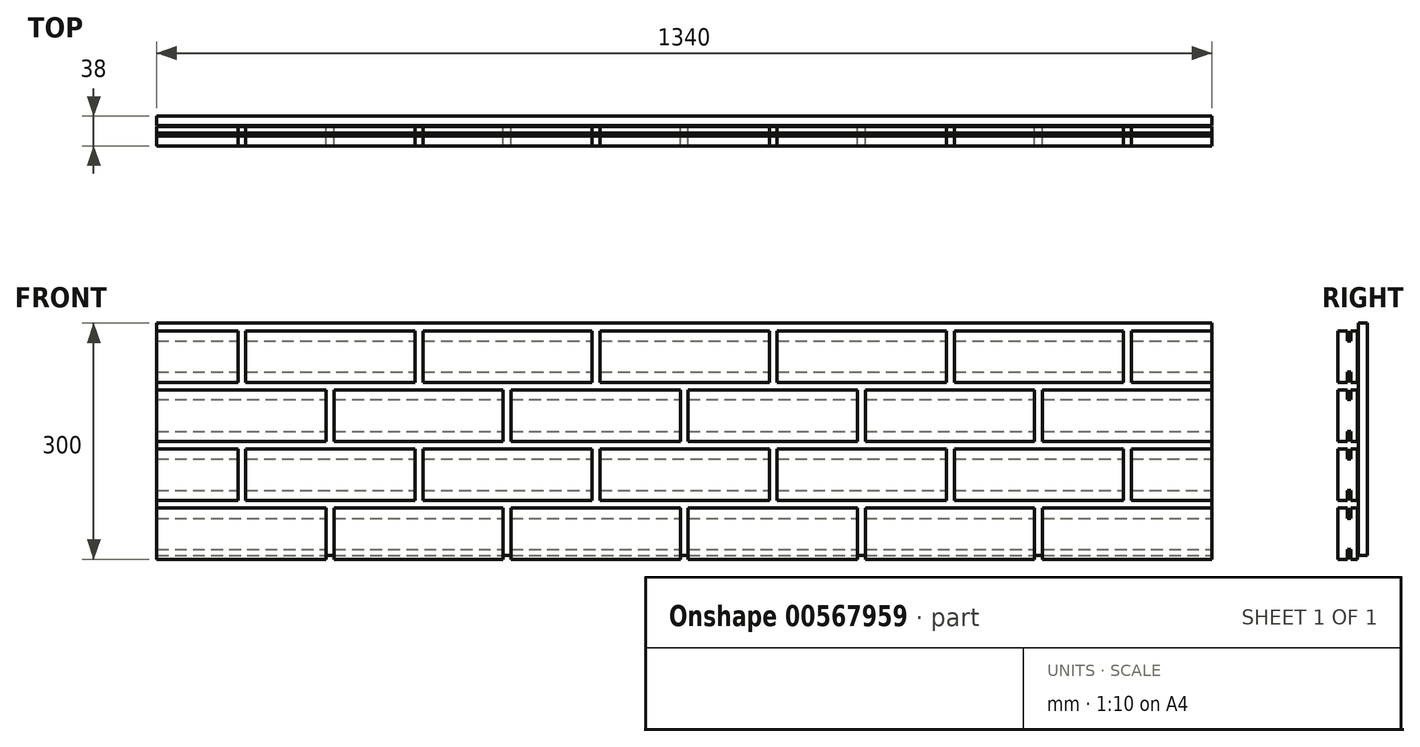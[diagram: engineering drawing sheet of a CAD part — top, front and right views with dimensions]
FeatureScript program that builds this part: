
annotation { "Feature Type Name" : "Feature", "Feature Type Description" : "" }
export const myFeature = defineFeature(function(context is Context, id is Id, definition is map)
    precondition{}
    {
        {
            var Q0;
            Q0=qCreatedBy(makeId("Front.planeOp"),FACE);
            var sketch = newSketch(context, id + "F0", { "sketchPlane" : qUnion([Q0])});
            skLineSegment(sketch, "E0", {"start": v(-1965.67, 0) * mm, "end": v(-1750.67, 0) * mm});
            skLineSegment(sketch, "E1", {"start": v(-1750.67, 0) * mm, "end": v(-1750.67, 65) * mm});
            skLineSegment(sketch, "E2", {"start": v(-1750.67, 65) * mm, "end": v(-1965.67, 65) * mm});
            skLineSegment(sketch, "E3", {"start": v(-1965.67, 65) * mm, "end": v(-1965.67, 0) * mm});
            skLineSegment(sketch, "E4", {"start": v(-1975.67, 0) * mm, "end": v(-2190.67, 0) * mm});
            skLineSegment(sketch, "E5", {"start": v(-2190.67, 0) * mm, "end": v(-2190.67, 65) * mm});
            skLineSegment(sketch, "E6", {"start": v(-2190.67, 65) * mm, "end": v(-1975.67, 65) * mm});
            skLineSegment(sketch, "E7", {"start": v(-1975.67, 65) * mm, "end": v(-1975.67, 0) * mm});
            skLineSegment(sketch, "E8", {"start": v(-2200.67, 0) * mm, "end": v(-2415.67, 0) * mm});
            skLineSegment(sketch, "E9", {"start": v(-2415.67, 0) * mm, "end": v(-2415.67, 65) * mm});
            skLineSegment(sketch, "E10", {"start": v(-2415.67, 65) * mm, "end": v(-2200.67, 65) * mm});
            skLineSegment(sketch, "E11", {"start": v(-2200.67, 65) * mm, "end": v(-2200.67, 0) * mm});
            skLineSegment(sketch, "E12", {"start": v(-2087.7, 139.95) * mm, "end": v(-2302.7, 139.95) * mm});
            skLineSegment(sketch, "E13", {"start": v(-2302.7, 139.95) * mm, "end": v(-2302.7, 74.95) * mm});
            skLineSegment(sketch, "E14", {"start": v(-2302.7, 74.95) * mm, "end": v(-2087.7, 74.95) * mm});
            skLineSegment(sketch, "E15", {"start": v(-2087.7, 74.95) * mm, "end": v(-2087.7, 139.95) * mm});
            skLineSegment(sketch, "E16", {"start": v(-2077.7, 139.95) * mm, "end": v(-1862.7, 139.95) * mm});
            skLineSegment(sketch, "E17", {"start": v(-1862.7, 139.95) * mm, "end": v(-1862.7, 74.95) * mm});
            skLineSegment(sketch, "E18", {"start": v(-1862.7, 74.95) * mm, "end": v(-2077.7, 74.95) * mm});
            skLineSegment(sketch, "E19", {"start": v(-2077.7, 74.95) * mm, "end": v(-2077.7, 139.95) * mm});
            skLineSegment(sketch, "E20", {"start": v(-1852.7, 139.95) * mm, "end": v(-1637.7, 139.95) * mm});
            skLineSegment(sketch, "E21", {"start": v(-1637.7, 139.95) * mm, "end": v(-1637.7, 74.95) * mm});
            skLineSegment(sketch, "E22", {"start": v(-1637.7, 74.95) * mm, "end": v(-1852.7, 74.95) * mm});
            skLineSegment(sketch, "E23", {"start": v(-1852.7, 74.95) * mm, "end": v(-1852.7, 139.95) * mm});
            skLineSegment(sketch, "E24", {"start": v(-2415.7, 139.95) * mm, "end": v(-2312.7, 139.95) * mm});
            skLineSegment(sketch, "E25", {"start": v(-2312.7, 139.95) * mm, "end": v(-2312.7, 74.95) * mm});
            skLineSegment(sketch, "E26", {"start": v(-2312.7, 74.95) * mm, "end": v(-2415.7, 74.95) * mm});
            skLineSegment(sketch, "E27", {"start": v(-2415.7, 74.95) * mm, "end": v(-2415.7, 139.95) * mm});
            skLineSegment(sketch, "E28", {"start": v(-1965.67, 215) * mm, "end": v(-1750.67, 215) * mm});
            skLineSegment(sketch, "E29", {"start": v(-1750.67, 215) * mm, "end": v(-1750.67, 150) * mm});
            skLineSegment(sketch, "E30", {"start": v(-1750.67, 150) * mm, "end": v(-1965.67, 150) * mm});
            skLineSegment(sketch, "E31", {"start": v(-1965.67, 150) * mm, "end": v(-1965.67, 215) * mm});
            skLineSegment(sketch, "E32", {"start": v(-1975.67, 215) * mm, "end": v(-2190.67, 215) * mm});
            skLineSegment(sketch, "E33", {"start": v(-2190.67, 215) * mm, "end": v(-2190.67, 150) * mm});
            skLineSegment(sketch, "E34", {"start": v(-2190.67, 150) * mm, "end": v(-1975.67, 150) * mm});
            skLineSegment(sketch, "E35", {"start": v(-1975.67, 150) * mm, "end": v(-1975.67, 215) * mm});
            skLineSegment(sketch, "E36", {"start": v(-2200.67, 215) * mm, "end": v(-2415.67, 215) * mm});
            skLineSegment(sketch, "E37", {"start": v(-2415.67, 215) * mm, "end": v(-2415.67, 150) * mm});
            skLineSegment(sketch, "E38", {"start": v(-2415.67, 150) * mm, "end": v(-2200.67, 150) * mm});
            skLineSegment(sketch, "E39", {"start": v(-2200.67, 150) * mm, "end": v(-2200.67, 215) * mm});
            skLineSegment(sketch, "E40", {"start": v(-2087.7, 224.95) * mm, "end": v(-2302.7, 224.95) * mm});
            skLineSegment(sketch, "E41", {"start": v(-2302.7, 224.95) * mm, "end": v(-2302.7, 289.95) * mm});
            skLineSegment(sketch, "E42", {"start": v(-2302.7, 289.95) * mm, "end": v(-2087.7, 289.95) * mm});
            skLineSegment(sketch, "E43", {"start": v(-2087.7, 289.95) * mm, "end": v(-2087.7, 224.95) * mm});
            skLineSegment(sketch, "E44", {"start": v(-2077.7, 224.95) * mm, "end": v(-1862.7, 224.95) * mm});
            skLineSegment(sketch, "E45", {"start": v(-1862.7, 224.95) * mm, "end": v(-1862.7, 289.95) * mm});
            skLineSegment(sketch, "E46", {"start": v(-1862.7, 289.95) * mm, "end": v(-2077.7, 289.95) * mm});
            skLineSegment(sketch, "E47", {"start": v(-2077.7, 289.95) * mm, "end": v(-2077.7, 224.95) * mm});
            skLineSegment(sketch, "E48", {"start": v(-1852.7, 224.95) * mm, "end": v(-1637.7, 224.95) * mm});
            skLineSegment(sketch, "E49", {"start": v(-1637.7, 224.95) * mm, "end": v(-1637.7, 289.95) * mm});
            skLineSegment(sketch, "E50", {"start": v(-1637.7, 289.95) * mm, "end": v(-1852.7, 289.95) * mm});
            skLineSegment(sketch, "E51", {"start": v(-1852.7, 289.95) * mm, "end": v(-1852.7, 224.95) * mm});
            skLineSegment(sketch, "E52", {"start": v(-2415.7, 224.95) * mm, "end": v(-2312.7, 224.95) * mm});
            skLineSegment(sketch, "E53", {"start": v(-2312.7, 224.95) * mm, "end": v(-2312.7, 289.95) * mm});
            skLineSegment(sketch, "E54", {"start": v(-2312.7, 289.95) * mm, "end": v(-2415.7, 289.95) * mm});
            skLineSegment(sketch, "E55", {"start": v(-2415.7, 289.95) * mm, "end": v(-2415.7, 224.95) * mm});
            skLineSegment(sketch, "E56", {"start": v(-1515.67, 0) * mm, "end": v(-1300.67, 0) * mm});
            skLineSegment(sketch, "E57", {"start": v(-1300.67, 0) * mm, "end": v(-1300.67, 65) * mm});
            skLineSegment(sketch, "E58", {"start": v(-1300.67, 65) * mm, "end": v(-1515.67, 65) * mm});
            skLineSegment(sketch, "E59", {"start": v(-1515.67, 65) * mm, "end": v(-1515.67, 0) * mm});
            skLineSegment(sketch, "E60", {"start": v(-1525.67, 0) * mm, "end": v(-1740.67, 0) * mm});
            skLineSegment(sketch, "E61", {"start": v(-1740.67, 0) * mm, "end": v(-1740.67, 65) * mm});
            skLineSegment(sketch, "E62", {"start": v(-1740.67, 65) * mm, "end": v(-1525.67, 65) * mm});
            skLineSegment(sketch, "E63", {"start": v(-1525.67, 65) * mm, "end": v(-1525.67, 0) * mm});
            skLineSegment(sketch, "E64", {"start": v(-1515.67, 215) * mm, "end": v(-1300.67, 215) * mm});
            skLineSegment(sketch, "E65", {"start": v(-1300.67, 215) * mm, "end": v(-1300.67, 150) * mm});
            skLineSegment(sketch, "E66", {"start": v(-1300.67, 150) * mm, "end": v(-1515.67, 150) * mm});
            skLineSegment(sketch, "E67", {"start": v(-1515.67, 150) * mm, "end": v(-1515.67, 215) * mm});
            skLineSegment(sketch, "E68", {"start": v(-1525.67, 215) * mm, "end": v(-1740.67, 215) * mm});
            skLineSegment(sketch, "E69", {"start": v(-1740.67, 215) * mm, "end": v(-1740.67, 150) * mm});
            skLineSegment(sketch, "E70", {"start": v(-1740.67, 150) * mm, "end": v(-1525.67, 150) * mm});
            skLineSegment(sketch, "E71", {"start": v(-1525.67, 150) * mm, "end": v(-1525.67, 215) * mm});
            skLineSegment(sketch, "E72", {"start": v(-1290.67, 0) * mm, "end": v(-1075.67, 0) * mm});
            skLineSegment(sketch, "E73", {"start": v(-1075.67, 0) * mm, "end": v(-1075.67, 65) * mm});
            skLineSegment(sketch, "E74", {"start": v(-1075.67, 65) * mm, "end": v(-1290.67, 65) * mm});
            skLineSegment(sketch, "E75", {"start": v(-1290.67, 65) * mm, "end": v(-1290.67, 0) * mm});
            skLineSegment(sketch, "E76", {"start": v(-1290.67, 150) * mm, "end": v(-1075.67, 150) * mm});
            skLineSegment(sketch, "E77", {"start": v(-1075.67, 150) * mm, "end": v(-1075.67, 215) * mm});
            skLineSegment(sketch, "E78", {"start": v(-1075.67, 215) * mm, "end": v(-1290.67, 215) * mm});
            skLineSegment(sketch, "E79", {"start": v(-1290.67, 215) * mm, "end": v(-1290.67, 150) * mm});
            skLineSegment(sketch, "E80", {"start": v(-1627.7, 139.95) * mm, "end": v(-1412.7, 139.95) * mm});
            skLineSegment(sketch, "E81", {"start": v(-1412.7, 139.95) * mm, "end": v(-1412.7, 74.95) * mm});
            skLineSegment(sketch, "E82", {"start": v(-1412.7, 74.95) * mm, "end": v(-1627.7, 74.95) * mm});
            skLineSegment(sketch, "E83", {"start": v(-1627.7, 74.95) * mm, "end": v(-1627.7, 139.95) * mm});
            skLineSegment(sketch, "E84", {"start": v(-1627.7, 224.95) * mm, "end": v(-1412.7, 224.95) * mm});
            skLineSegment(sketch, "E85", {"start": v(-1412.7, 224.95) * mm, "end": v(-1412.7, 289.95) * mm});
            skLineSegment(sketch, "E86", {"start": v(-1412.7, 289.95) * mm, "end": v(-1627.7, 289.95) * mm});
            skLineSegment(sketch, "E87", {"start": v(-1627.7, 289.95) * mm, "end": v(-1627.7, 224.95) * mm});
            skLineSegment(sketch, "E88", {"start": v(-1402.7, 139.95) * mm, "end": v(-1187.7, 139.95) * mm});
            skLineSegment(sketch, "E89", {"start": v(-1187.7, 139.95) * mm, "end": v(-1187.7, 74.95) * mm});
            skLineSegment(sketch, "E90", {"start": v(-1187.7, 74.95) * mm, "end": v(-1402.7, 74.95) * mm});
            skLineSegment(sketch, "E91", {"start": v(-1402.7, 74.95) * mm, "end": v(-1402.7, 139.95) * mm});
            skLineSegment(sketch, "E92", {"start": v(-1402.7, 224.95) * mm, "end": v(-1187.7, 224.95) * mm});
            skLineSegment(sketch, "E93", {"start": v(-1187.7, 224.95) * mm, "end": v(-1187.7, 289.95) * mm});
            skLineSegment(sketch, "E94", {"start": v(-1187.7, 289.95) * mm, "end": v(-1402.7, 289.95) * mm});
            skLineSegment(sketch, "E95", {"start": v(-1402.7, 289.95) * mm, "end": v(-1402.7, 224.95) * mm});
            skLineSegment(sketch, "E96", {"start": v(-1177.7, 139.95) * mm, "end": v(-1075.67, 139.95) * mm});
            skLineSegment(sketch, "E97", {"start": v(-1075.67, 139.95) * mm, "end": v(-1075.67, 74.95) * mm});
            skLineSegment(sketch, "E98", {"start": v(-1075.67, 74.95) * mm, "end": v(-1177.7, 74.95) * mm});
            skLineSegment(sketch, "E99", {"start": v(-1177.7, 74.95) * mm, "end": v(-1177.7, 139.95) * mm});
            skLineSegment(sketch, "E100", {"start": v(-1177.7, 224.95) * mm, "end": v(-1075.67, 224.95) * mm});
            skLineSegment(sketch, "E101", {"start": v(-1075.67, 224.95) * mm, "end": v(-1075.67, 289.95) * mm});
            skLineSegment(sketch, "E102", {"start": v(-1075.67, 289.95) * mm, "end": v(-1177.7, 289.95) * mm});
            skLineSegment(sketch, "E103", {"start": v(-1177.7, 289.95) * mm, "end": v(-1177.7, 224.95) * mm});
            skLineSegment(sketch, "E104", {"start": v(-2415.67, 5) * mm, "end": v(-1075.67, 5) * mm});
            skLineSegment(sketch, "E105", {"start": v(-1075.67, 5) * mm, "end": v(-1075.67, 300) * mm});
            skLineSegment(sketch, "E106", {"start": v(-1075.67, 300) * mm, "end": v(-2415.67, 300) * mm});
            skLineSegment(sketch, "E107", {"start": v(-2415.67, 300) * mm, "end": v(-2415.67, 5) * mm});
            skSolve(sketch);
        }
        {
            var Q0;
            {var subQ0=sQuery(id+"F0.wireOp",EDGE,"E8");Q0=makeQuery(id+"F0.imprint","IMPRINT",FACE,{"disambiguationData":[TD([[makeQuery(id+"F0.imprint","IMPRINT",EDGE,{"derivedFrom":subQ0}),-1.0]])]});}
            var Q1;
            {var subQ0=sQuery(id+"F0.wireOp",EDGE,"E4");Q1=makeQuery(id+"F0.imprint","IMPRINT",FACE,{"disambiguationData":[TD([[makeQuery(id+"F0.imprint","IMPRINT",EDGE,{"derivedFrom":subQ0}),-1.0]])]});}
            var Q2;
            {var subQ0=sQuery(id+"F0.wireOp",EDGE,"E0");Q2=makeQuery(id+"F0.imprint","IMPRINT",FACE,{"disambiguationData":[TD([[makeQuery(id+"F0.imprint","IMPRINT",EDGE,{"derivedFrom":subQ0}),1.0]])]});}
            var Q3;
            {var subQ0=sQuery(id+"F0.wireOp",EDGE,"E60");Q3=makeQuery(id+"F0.imprint","IMPRINT",FACE,{"disambiguationData":[TD([[makeQuery(id+"F0.imprint","IMPRINT",EDGE,{"derivedFrom":subQ0}),-1.0]])]});}
            var Q4;
            {var subQ0=sQuery(id+"F0.wireOp",EDGE,"E56");Q4=makeQuery(id+"F0.imprint","IMPRINT",FACE,{"disambiguationData":[TD([[makeQuery(id+"F0.imprint","IMPRINT",EDGE,{"derivedFrom":subQ0}),1.0]])]});}
            var Q5;
            {var subQ0=sQuery(id+"F0.wireOp",EDGE,"E72");Q5=makeQuery(id+"F0.imprint","IMPRINT",FACE,{"disambiguationData":[TD([[makeQuery(id+"F0.imprint","IMPRINT",EDGE,{"derivedFrom":subQ0}),1.0]])]});}
            var Q6;
            {var subQ0=sQuery(id+"F0.wireOp",EDGE,"E74");Q6=makeQuery(id+"F0.imprint","IMPRINT",FACE,{"disambiguationData":[TD([[makeQuery(id+"F0.imprint","IMPRINT",EDGE,{"derivedFrom":subQ0}),1.0]])]});}
            var Q7;
            {var subQ0=sQuery(id+"F0.wireOp",EDGE,"E58");Q7=makeQuery(id+"F0.imprint","IMPRINT",FACE,{"disambiguationData":[TD([[makeQuery(id+"F0.imprint","IMPRINT",EDGE,{"derivedFrom":subQ0}),1.0]])]});}
            var Q8;
            {var subQ0=sQuery(id+"F0.wireOp",EDGE,"E62");Q8=makeQuery(id+"F0.imprint","IMPRINT",FACE,{"disambiguationData":[TD([[makeQuery(id+"F0.imprint","IMPRINT",EDGE,{"derivedFrom":subQ0}),-1.0]])]});}
            var Q9;
            {var subQ0=sQuery(id+"F0.wireOp",EDGE,"E2");Q9=makeQuery(id+"F0.imprint","IMPRINT",FACE,{"disambiguationData":[TD([[makeQuery(id+"F0.imprint","IMPRINT",EDGE,{"derivedFrom":subQ0}),1.0]])]});}
            var Q10;
            {var subQ0=sQuery(id+"F0.wireOp",EDGE,"E6");Q10=makeQuery(id+"F0.imprint","IMPRINT",FACE,{"disambiguationData":[TD([[makeQuery(id+"F0.imprint","IMPRINT",EDGE,{"derivedFrom":subQ0}),-1.0]])]});}
            var Q11;
            {var subQ0=sQuery(id+"F0.wireOp",EDGE,"E10");Q11=makeQuery(id+"F0.imprint","IMPRINT",FACE,{"disambiguationData":[TD([[makeQuery(id+"F0.imprint","IMPRINT",EDGE,{"derivedFrom":subQ0}),-1.0]])]});}
            var Q12;
            {var subQ0=sQuery(id+"F0.wireOp",EDGE,"E25");Q12=makeQuery(id+"F0.imprint","IMPRINT",FACE,{"disambiguationData":[TD([[makeQuery(id+"F0.imprint","IMPRINT",EDGE,{"derivedFrom":subQ0}),-1.0]])]});}
            var Q13;
            Q13=makeQuery(id+"F0.imprint","IMPRINT",FACE,{"disambiguationData":[TD([[makeQuery(id+"F0.imprint","IMPRINT",EDGE,{"derivedFrom":sQuery(id+"F0.wireOp",EDGE,"E12")}),1.0]])]});
            var Q14;
            Q14=makeQuery(id+"F0.imprint","IMPRINT",FACE,{"disambiguationData":[TD([[makeQuery(id+"F0.imprint","IMPRINT",EDGE,{"derivedFrom":sQuery(id+"F0.wireOp",EDGE,"E16")}),-1.0]])]});
            var Q15;
            Q15=makeQuery(id+"F0.imprint","IMPRINT",FACE,{"disambiguationData":[TD([[makeQuery(id+"F0.imprint","IMPRINT",EDGE,{"derivedFrom":sQuery(id+"F0.wireOp",EDGE,"E20")}),-1.0]])]});
            var Q16;
            Q16=makeQuery(id+"F0.imprint","IMPRINT",FACE,{"disambiguationData":[TD([[makeQuery(id+"F0.imprint","IMPRINT",EDGE,{"derivedFrom":sQuery(id+"F0.wireOp",EDGE,"E80")}),-1.0]])]});
            var Q17;
            Q17=makeQuery(id+"F0.imprint","IMPRINT",FACE,{"disambiguationData":[TD([[makeQuery(id+"F0.imprint","IMPRINT",EDGE,{"derivedFrom":sQuery(id+"F0.wireOp",EDGE,"E88")}),-1.0]])]});
            var Q18;
            {var subQ0=sQuery(id+"F0.wireOp",EDGE,"E96");Q18=makeQuery(id+"F0.imprint","IMPRINT",FACE,{"disambiguationData":[TD([[makeQuery(id+"F0.imprint","IMPRINT",EDGE,{"derivedFrom":subQ0}),-1.0]])]});}
            var Q19;
            {var subQ0=sQuery(id+"F0.wireOp",EDGE,"E76");Q19=makeQuery(id+"F0.imprint","IMPRINT",FACE,{"disambiguationData":[TD([[makeQuery(id+"F0.imprint","IMPRINT",EDGE,{"derivedFrom":subQ0}),1.0]])]});}
            var Q20;
            Q20=makeQuery(id+"F0.imprint","IMPRINT",FACE,{"disambiguationData":[TD([[makeQuery(id+"F0.imprint","IMPRINT",EDGE,{"derivedFrom":sQuery(id+"F0.wireOp",EDGE,"E64")}),-1.0]])]});
            var Q21;
            Q21=makeQuery(id+"F0.imprint","IMPRINT",FACE,{"disambiguationData":[TD([[makeQuery(id+"F0.imprint","IMPRINT",EDGE,{"derivedFrom":sQuery(id+"F0.wireOp",EDGE,"E68")}),1.0]])]});
            var Q22;
            Q22=makeQuery(id+"F0.imprint","IMPRINT",FACE,{"disambiguationData":[TD([[makeQuery(id+"F0.imprint","IMPRINT",EDGE,{"derivedFrom":sQuery(id+"F0.wireOp",EDGE,"E28")}),-1.0]])]});
            var Q23;
            {var subQ0=sQuery(id+"F0.wireOp",EDGE,"E36");Q23=makeQuery(id+"F0.imprint","IMPRINT",FACE,{"disambiguationData":[TD([[makeQuery(id+"F0.imprint","IMPRINT",EDGE,{"derivedFrom":subQ0}),1.0]])]});}
            var Q24;
            Q24=makeQuery(id+"F0.imprint","IMPRINT",FACE,{"disambiguationData":[TD([[makeQuery(id+"F0.imprint","IMPRINT",EDGE,{"derivedFrom":sQuery(id+"F0.wireOp",EDGE,"E32")}),1.0]])]});
            var Q25;
            {var subQ0=sQuery(id+"F0.wireOp",EDGE,"E53");Q25=makeQuery(id+"F0.imprint","IMPRINT",FACE,{"disambiguationData":[TD([[makeQuery(id+"F0.imprint","IMPRINT",EDGE,{"derivedFrom":subQ0}),1.0]])]});}
            var Q26;
            Q26=makeQuery(id+"F0.imprint","IMPRINT",FACE,{"disambiguationData":[TD([[makeQuery(id+"F0.imprint","IMPRINT",EDGE,{"derivedFrom":sQuery(id+"F0.wireOp",EDGE,"E40")}),-1.0]])]});
            var Q27;
            Q27=makeQuery(id+"F0.imprint","IMPRINT",FACE,{"disambiguationData":[TD([[makeQuery(id+"F0.imprint","IMPRINT",EDGE,{"derivedFrom":sQuery(id+"F0.wireOp",EDGE,"E44")}),1.0]])]});
            var Q28;
            Q28=makeQuery(id+"F0.imprint","IMPRINT",FACE,{"disambiguationData":[TD([[makeQuery(id+"F0.imprint","IMPRINT",EDGE,{"derivedFrom":sQuery(id+"F0.wireOp",EDGE,"E48")}),1.0]])]});
            var Q29;
            Q29=makeQuery(id+"F0.imprint","IMPRINT",FACE,{"disambiguationData":[TD([[makeQuery(id+"F0.imprint","IMPRINT",EDGE,{"derivedFrom":sQuery(id+"F0.wireOp",EDGE,"E84")}),1.0]])]});
            var Q30;
            Q30=makeQuery(id+"F0.imprint","IMPRINT",FACE,{"disambiguationData":[TD([[makeQuery(id+"F0.imprint","IMPRINT",EDGE,{"derivedFrom":sQuery(id+"F0.wireOp",EDGE,"E92")}),1.0]])]});
            var Q31;
            {var subQ0=sQuery(id+"F0.wireOp",EDGE,"E100");Q31=makeQuery(id+"F0.imprint","IMPRINT",FACE,{"disambiguationData":[TD([[makeQuery(id+"F0.imprint","IMPRINT",EDGE,{"derivedFrom":subQ0}),1.0]])]});}
            extrude(context, id + "F1", {"entities" : qUnion([Q0, Q1, Q2, Q3, Q4, Q5, Q6, Q7, Q8, Q9, Q10, Q11, Q12, Q13, Q14, Q15, Q16, Q17, Q18, Q19, Q20, Q21, Q22, Q23, Q24, Q25, Q26, Q27, Q28, Q29, Q30, Q31]), "depth" : 25 * mm, "offsetDistance" : 25 * mm});
        }
        {
            var Q0;
            Q0=makeQuery(id+"F1.opExtrude","SWEPT_FACE",FACE,{"disambiguationData":[OSD([sQuery(id+"F0.wireOp",EDGE,"E73"),sQuery(id+"F0.wireOp",EDGE,"E105")])]});
            cPlane(context, id + "F2", {"entities" : qUnion([Q0]), "cplaneType" : CPlaneType.OFFSET, "offset" : 0 * mm, "width" : 150 * mm, "height" : 150 * mm});
        }
        {
            var Q0;
            Q0=qCreatedBy(id+"F2.planeOp",FACE);
            var sketch = newSketch(context, id + "F3", { "sketchPlane" : qUnion([Q0])});
            skLineSegment(sketch, "E108.bottom", {"start": v(-12.5, 52.26) * mm, "end": v(-8.5, 52.26) * mm});
            skLineSegment(sketch, "E108.top", {"start": v(-12.5, 87.26) * mm, "end": v(-8.5, 87.26) * mm});
            skLineSegment(sketch, "E108.left", {"start": v(-12.5, 52.26) * mm, "end": v(-12.5, 87.26) * mm});
            skLineSegment(sketch, "E108.right", {"start": v(-8.5, 52.26) * mm, "end": v(-8.5, 87.26) * mm});
            skLineSegment(sketch, "E109.bottom", {"start": v(-12.5, 127.29) * mm, "end": v(-8.5, 127.29) * mm});
            skLineSegment(sketch, "E109.top", {"start": v(-12.5, 162.29) * mm, "end": v(-8.5, 162.29) * mm});
            skLineSegment(sketch, "E109.left", {"start": v(-12.5, 127.29) * mm, "end": v(-12.5, 162.29) * mm});
            skLineSegment(sketch, "E109.right", {"start": v(-8.5, 127.29) * mm, "end": v(-8.5, 162.29) * mm});
            skLineSegment(sketch, "E110.bottom", {"start": v(-12.5, 202.92) * mm, "end": v(-8.5, 202.92) * mm});
            skLineSegment(sketch, "E110.top", {"start": v(-12.5, 237.92) * mm, "end": v(-8.5, 237.92) * mm});
            skLineSegment(sketch, "E110.left", {"start": v(-12.5, 202.92) * mm, "end": v(-12.5, 237.92) * mm});
            skLineSegment(sketch, "E110.right", {"start": v(-8.5, 202.92) * mm, "end": v(-8.5, 237.92) * mm});
            skLineSegment(sketch, "E111.bottom", {"start": v(-12.5, 0) * mm, "end": v(-8.5, 0) * mm});
            skLineSegment(sketch, "E111.top", {"start": v(-12.5, 12.75) * mm, "end": v(-8.5, 12.75) * mm});
            skLineSegment(sketch, "E111.left", {"start": v(-12.5, 0) * mm, "end": v(-12.5, 12.75) * mm});
            skLineSegment(sketch, "E111.right", {"start": v(-8.5, 0) * mm, "end": v(-8.5, 12.75) * mm});
            skLineSegment(sketch, "E112.bottom", {"start": v(-12.5, 277.2) * mm, "end": v(-8.5, 277.2) * mm});
            skLineSegment(sketch, "E112.top", {"start": v(-12.5, 289.95) * mm, "end": v(-8.5, 289.95) * mm});
            skLineSegment(sketch, "E112.left", {"start": v(-12.5, 277.2) * mm, "end": v(-12.5, 289.95) * mm});
            skLineSegment(sketch, "E112.right", {"start": v(-8.5, 277.2) * mm, "end": v(-8.5, 289.95) * mm});
            skSolve(sketch);
        }
        {
            var Q0;
            Q0 = qSketchRegion(id + "F3", true);
            extrude(context, id + "F4", {"entities" : qUnion([Q0]), "operationType" : NewBodyOperationType.REMOVE, "endBound" : BoundingType.THROUGH_ALL, "oppositeDirection" : true, "depth" : 25 * mm, "offsetDistance" : 25 * mm});
        }
        {
            var Q0;
            Q0=qCreatedBy(id+"F2.planeOp",FACE);
            var sketch = newSketch(context, id + "F5", { "sketchPlane" : qUnion([Q0])});
            skLineSegment(sketch, "E113.bottom", {"start": v(1, 5) * mm, "end": v(13, 5) * mm});
            skLineSegment(sketch, "E113.top", {"start": v(1, 300) * mm, "end": v(13, 300) * mm});
            skLineSegment(sketch, "E113.left", {"start": v(1, 5) * mm, "end": v(1, 300) * mm});
            skLineSegment(sketch, "E113.right", {"start": v(13, 5) * mm, "end": v(13, 300) * mm});
            skSolve(sketch);
        }
        {
            var Q0;
            Q0 = qSketchRegion(id + "F5", true);
            extrude(context, id + "F6", {"entities" : qUnion([Q0]), "oppositeDirection" : true, "depth" : 1340 * mm, "offsetDistance" : 25 * mm});
        }
    });
